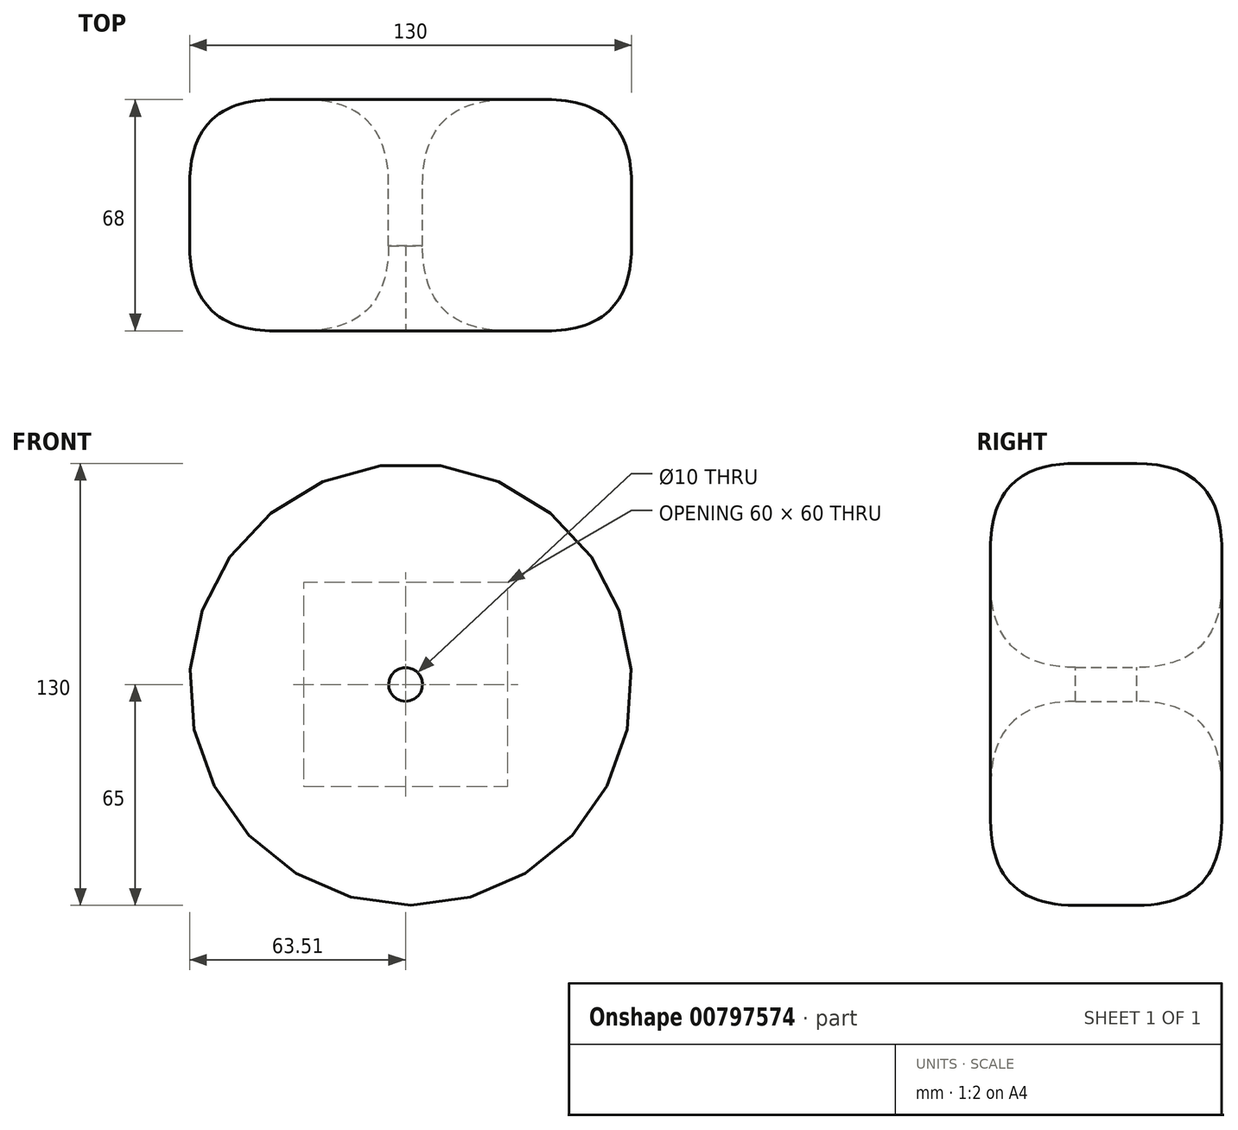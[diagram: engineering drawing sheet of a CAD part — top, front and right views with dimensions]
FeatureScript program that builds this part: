
annotation { "Feature Type Name" : "Feature", "Feature Type Description" : "" }
export const myFeature = defineFeature(function(context is Context, id is Id, definition is map)
    precondition{}
    {
        {
            var Q0;
            Q0=qCreatedBy(makeId("Front.planeOp"),FACE);
            var sketch = newSketch(context, id + "F0", { "sketchPlane" : qUnion([Q0])});
            skCircle(sketch, "E0", {"center": v(1.49, 0) * mm, "radius": 65 * mm});
            skCircle(sketch, "E1", {"center": v(0, 0) * mm, "radius": 5 * mm});
            skSolve(sketch);
        }
        {
            var Q0;
            Q0=qSketchRegion(id+"F0",true);
            var Q1;
            Q1=makeQuery(id+"F0.imprint","IMPRINT",FACE,{"disambiguationData":[TD([[makeQuery(id+"F0.imprint","IMPRINT",EDGE,{"derivedFrom":sQuery(id+"F0.wireOp",EDGE,"Xh3rmZ6r-mnXF-cQC0-qcFj-POpnVeDtVYFI")}),1.0]])]});
            extrude(context, id + "F1", {"entities" : qUnion([Q0, Q1]), "depth" : 68 * mm, "offsetDistance" : 25 * mm});
        }
        {
            var Q0;
            Q0=makeQuery(id+"F1.opExtrude","CAP_EDGE",EDGE,{"disambiguationData":[OSD([sQuery(id+"F0.wireOp",EDGE,"E0")])],"isStart":false});
            var Q1;
            Q1=makeQuery(id+"F1.opExtrude","CAP_EDGE",EDGE,{"disambiguationData":[OSD([sQuery(id+"F0.wireOp",EDGE,"E0")])],"isStart":true});
            var Q2;
            Q2=makeQuery(id+"F1.opExtrude","CAP_EDGE",EDGE,{"disambiguationData":[OSD([sQuery(id+"F0.wireOp",EDGE,"E1")])],"isStart":false});
            var Q3;
            Q3=makeQuery(id+"F1.opExtrude","CAP_EDGE",EDGE,{"disambiguationData":[OSD([sQuery(id+"F0.wireOp",EDGE,"E1")])],"isStart":true});
            fillet(context, id + "F2", {"entities" : qUnion([Q0, Q1, Q2, Q3]), "radius" : 25 * mm, "tangentPropagation" : true, "rho" : 0.5, "crossSection" : FilletCrossSection.CONIC, "allowEdgeOverflow" : false});
        }
    });
